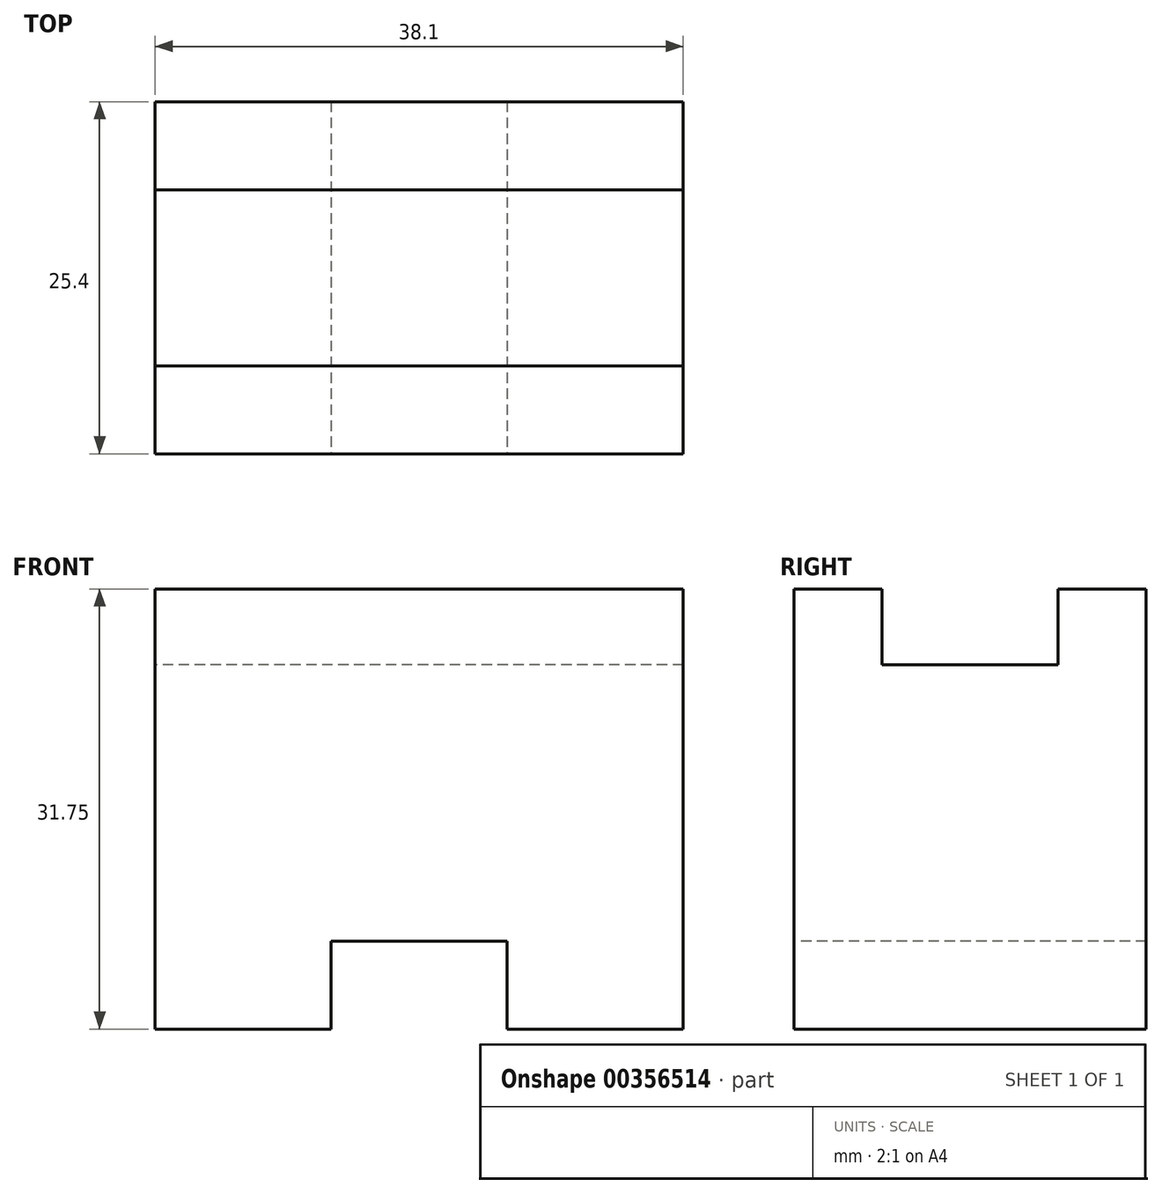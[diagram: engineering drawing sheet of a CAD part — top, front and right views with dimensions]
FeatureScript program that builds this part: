
annotation { "Feature Type Name" : "Feature", "Feature Type Description" : "" }
export const myFeature = defineFeature(function(context is Context, id is Id, definition is map)
    precondition{}
    {
        {
            var Q0;
            Q0=qCreatedBy(makeId("Right.planeOp"),FACE);
            var sketch = newSketch(context, id + "F0", { "sketchPlane" : qUnion([Q0])});
            skLineSegment(sketch, "E0", {"start": v(0, 0) * mm, "end": v(25.4, 0) * mm});
            skLineSegment(sketch, "E1", {"start": v(25.4, 0) * mm, "end": v(25.4, 31.75) * mm});
            skLineSegment(sketch, "E2", {"start": v(25.4, 31.75) * mm, "end": v(19.05, 31.75) * mm});
            skLineSegment(sketch, "E3", {"start": v(19.05, 31.75) * mm, "end": v(19.05, 26.29) * mm});
            skLineSegment(sketch, "E4", {"start": v(19.05, 26.29) * mm, "end": v(6.35, 26.29) * mm});
            skLineSegment(sketch, "E5", {"start": v(6.35, 26.29) * mm, "end": v(6.35, 31.75) * mm});
            skLineSegment(sketch, "E6", {"start": v(6.35, 31.75) * mm, "end": v(0, 31.75) * mm});
            skLineSegment(sketch, "E7", {"start": v(0, 31.75) * mm, "end": v(0, 0) * mm});
            skSolve(sketch);
        }
        {
            var Q0;
            Q0 = qSketchRegion(id + "F0", true);
            extrude(context, id + "F1", {"entities" : qUnion([Q0]), "depth" : 38.1 * mm});
        }
        {
            var Q0;
            Q0=makeQuery(id+"F1.opExtrude","SWEPT_FACE",FACE,{"disambiguationData":[OSD([sQuery(id+"F0.wireOp",EDGE,"E7")])]});
            var sketch = newSketch(context, id + "F2", { "sketchPlane" : qUnion([Q0])});
            skLineSegment(sketch, "E8", {"start": v(0, 0) * mm, "end": v(12.7, 0) * mm});
            skLineSegment(sketch, "E9", {"start": v(12.7, 0) * mm, "end": v(12.7, 6.35) * mm});
            skLineSegment(sketch, "E10", {"start": v(12.7, 6.35) * mm, "end": v(25.4, 6.35) * mm});
            skLineSegment(sketch, "E11", {"start": v(25.4, 6.35) * mm, "end": v(25.4, 0) * mm});
            skSolve(sketch);
        }
        {
            var Q0;
            {var subQ0=sQuery(id+"F2.wireOp",EDGE,"E9");Q0=makeQuery(id+"F2.imprint","IMPRINT",FACE,{"disambiguationData":[TD([[makeQuery(id+"F2.imprint","IMPRINT",EDGE,{"derivedFrom":subQ0}),-1.0]])]});}
            extrude(context, id + "F3", {"entities" : qUnion([Q0]), "operationType" : NewBodyOperationType.REMOVE, "oppositeDirection" : true, "depth" : 25.4 * mm});
        }
    });
